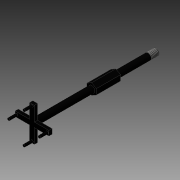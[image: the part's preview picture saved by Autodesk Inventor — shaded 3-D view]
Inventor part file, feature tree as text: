
AUTODESK INVENTOR PART (.ipt)
format: ipt  version: 2016 (Build 200138000, 138)  size: 162,816 bytes
history: native  units: mm
features: extrude x5, sketch x5, thread x1
ambient origin geometry x8: Origin, YZ Plane, XZ Plane, XY Plane, X Axis, Y Axis, Z Axis, Center Point
bodies: 实体1 (feature_tree)
feature tree (11):
  extrude  "拉伸1"  Depth=15.0mm
  extrude  "拉伸2"  Depth=5.0mm TaperAngle=0.0deg
  thread  "螺纹1"  [1 undecoded]
  extrude  "拉伸6"  Depth=35.0mm TaperAngle=0.0deg
  extrude  "拉伸7"  Depth=2.0mm TaperAngle=0.0deg
  extrude  "拉伸8"  Depth=5.0mm
  sketch  "草图1"  dims[d1=15.0mm d2=0.0mm d3=3.9mm]
  sketch  "草图2"  dims[d4=25.0mm d5=0.0mm d6=5.0mm d7=0.0mm d12=4.0mm]
  sketch  "草图6"  dims[d22=4.0mm d23=35.0mm d24=0.0mm]
  sketch  "草图7"  dims[d25=3.0mm d26=21.0mm d27=2.0mm d28=0.0mm]
  sketch  "草图8"  dims[d29=19.0mm d30=1.5mm d31=1.5mm d32=1.5mm d33=1.5mm d34=5.0mm d35=0.0mm]
note: 1 required parameter value undecoded (feature->parameter linkage not recoverable at this tier; creation-order binding heuristic only, values carry confidence <= 0.55)
